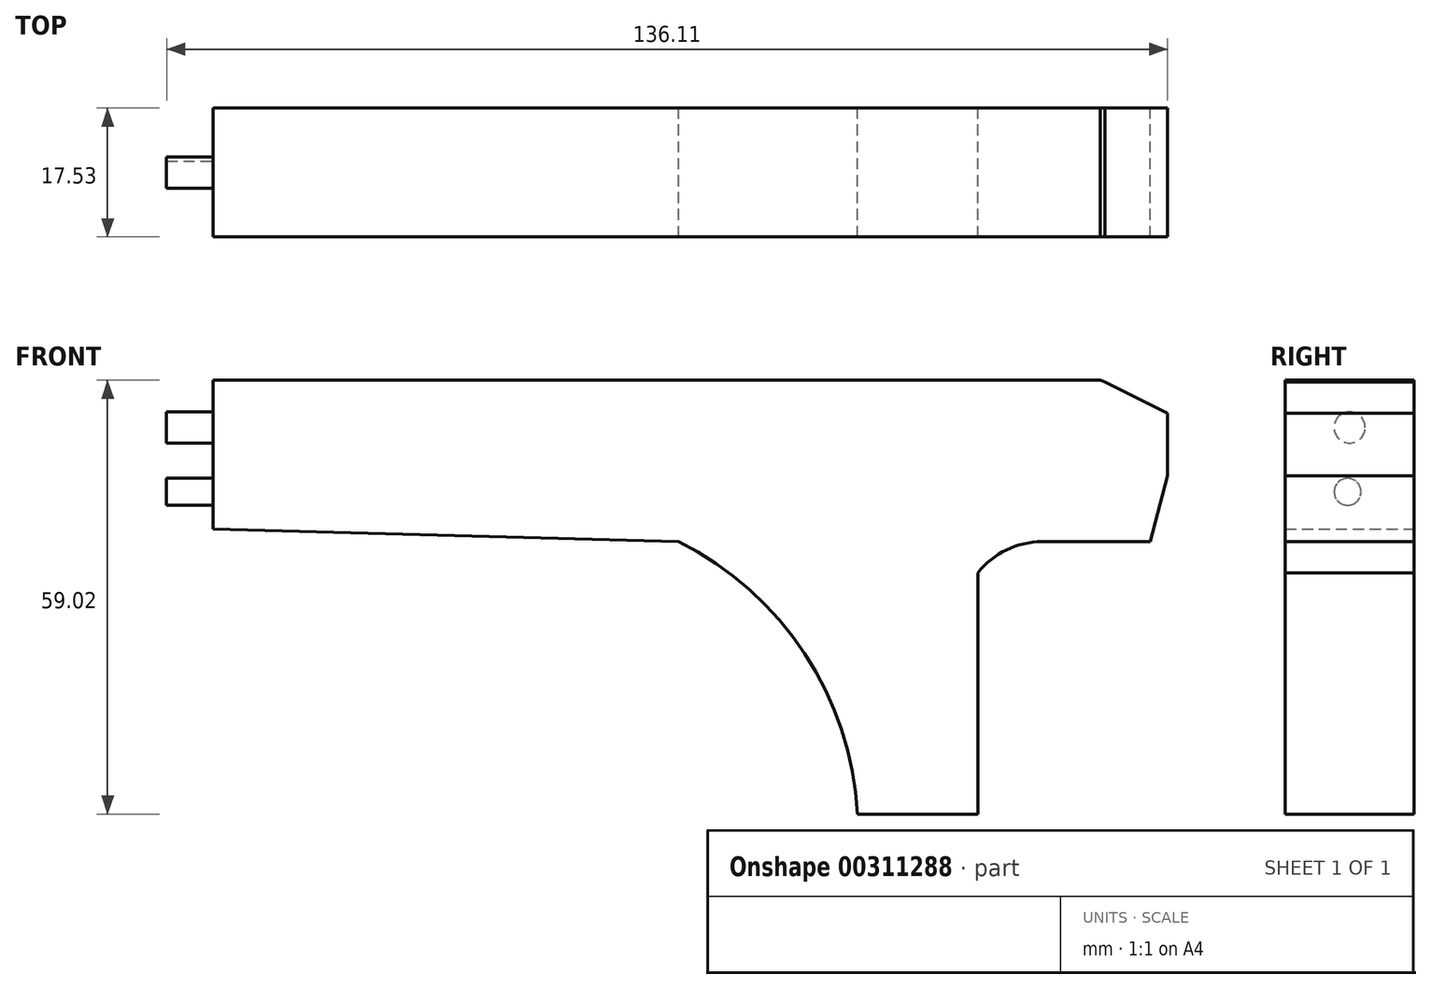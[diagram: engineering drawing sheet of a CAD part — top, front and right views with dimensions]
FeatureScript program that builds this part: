
annotation { "Feature Type Name" : "Feature", "Feature Type Description" : "" }
export const myFeature = defineFeature(function(context is Context, id is Id, definition is map)
    precondition{}
    {
        {
            var Q0;
            Q0=qCreatedBy(makeId("Front.planeOp"),FACE);
            var sketch = newSketch(context, id + "F0", { "sketchPlane" : qUnion([Q0])});
            skLineSegment(sketch, "E0", {"start": v(24.3, -42.08) * mm, "end": v(40.7, -42.08) * mm});
            skLineSegment(sketch, "E1", {"start": v(40.7, -42.08) * mm, "end": v(40.7, -9.27) * mm});
            skLineSegment(sketch, "E2", {"start": v(49.43, -5) * mm, "end": v(64.14, -5) * mm});
            skLineSegment(sketch, "E3", {"start": v(64.14, -5) * mm, "end": v(66.48, 3.94) * mm});
            skLineSegment(sketch, "E4", {"start": v(66.48, 3.94) * mm, "end": v(66.48, 12.46) * mm});
            skLineSegment(sketch, "E5", {"start": v(66.48, 12.46) * mm, "end": v(57.96, 16.73) * mm});
            skLineSegment(sketch, "E6", {"start": v(57.32, 16.94) * mm, "end": v(-63.28, 16.94) * mm});
            skLineSegment(sketch, "E7", {"start": v(-63.28, 16.94) * mm, "end": v(-63.28, -3.3) * mm});
            skLineSegment(sketch, "E8", {"start": v(-63.28, -3.3) * mm, "end": v(0, -5) * mm});
            skArc(sketch, "E9", {"start": v(49.43, -5) * mm, "mid": v(44.57, -6.13) * mm, "end": v(40.7, -9.27) * mm});
            skArc(sketch, "E10", {"start": v(24.3, -42.08) * mm, "mid": v(17.16, -20.26) * mm, "end": v(0, -5) * mm});
            skArc(sketch, "E11", {"start": v(-4.04, -4.9) * mm, "mid": v(-0.03, -16.94) * mm, "end": v(12.36, -14.17) * mm});
            skLineSegment(sketch, "E12", {"start": v(57.96, 16.73) * mm, "end": v(57.32, 16.94) * mm});
            skSolve(sketch);
        }
        {
            var Q0;
            {var subQ6=sQuery(id+"F0.wireOp",EDGE,"E0");Q0=makeQuery(id+"F0.imprint","IMPRINT",FACE,{"disambiguationData":[TD([[makeQuery(id+"F0.imprint","IMPRINT",EDGE,{"derivedFrom":subQ6}),1.0]])]});}
            extrude(context, id + "F1", {"entities" : qUnion([Q0]), "depth" : 17.53 * mm});
        }
        {
            var Q0;
            Q0=makeQuery(id+"F1.opExtrude","SWEPT_FACE",FACE,{"disambiguationData":[OSD([sQuery(id+"F0.wireOp",EDGE,"E7")])]});
            var sketch = newSketch(context, id + "F2", { "sketchPlane" : qUnion([Q0])});
            skCircle(sketch, "E13", {"center": v(8.76, 10.52) * mm, "radius": 2.11 * mm});
            skPoint(sketch, "E13.centerSnap0", {"position": v(8.76, 16.94) * mm});
            skCircle(sketch, "E14", {"center": v(9.03, 1.77) * mm, "radius": 1.83 * mm});
            skSolve(sketch);
        }
        {
            var Q0;
            Q0=makeQuery(id+"F2.imprint","IMPRINT",FACE,{"disambiguationData":[TD([[makeQuery(id+"F2.imprint","IMPRINT",EDGE,{"derivedFrom":sQuery(id+"F2.wireOp",EDGE,"E13")}),1.0]])]});
            var Q1;
            Q1=makeQuery(id+"F2.imprint","IMPRINT",FACE,{"disambiguationData":[TD([[makeQuery(id+"F2.imprint","IMPRINT",EDGE,{"derivedFrom":sQuery(id+"F2.wireOp",EDGE,"E14")}),1.0]])]});
            extrude(context, id + "F3", {"entities" : qUnion([Q0, Q1]), "operationType" : NewBodyOperationType.ADD, "depth" : 6.35 * mm});
        }
    });
